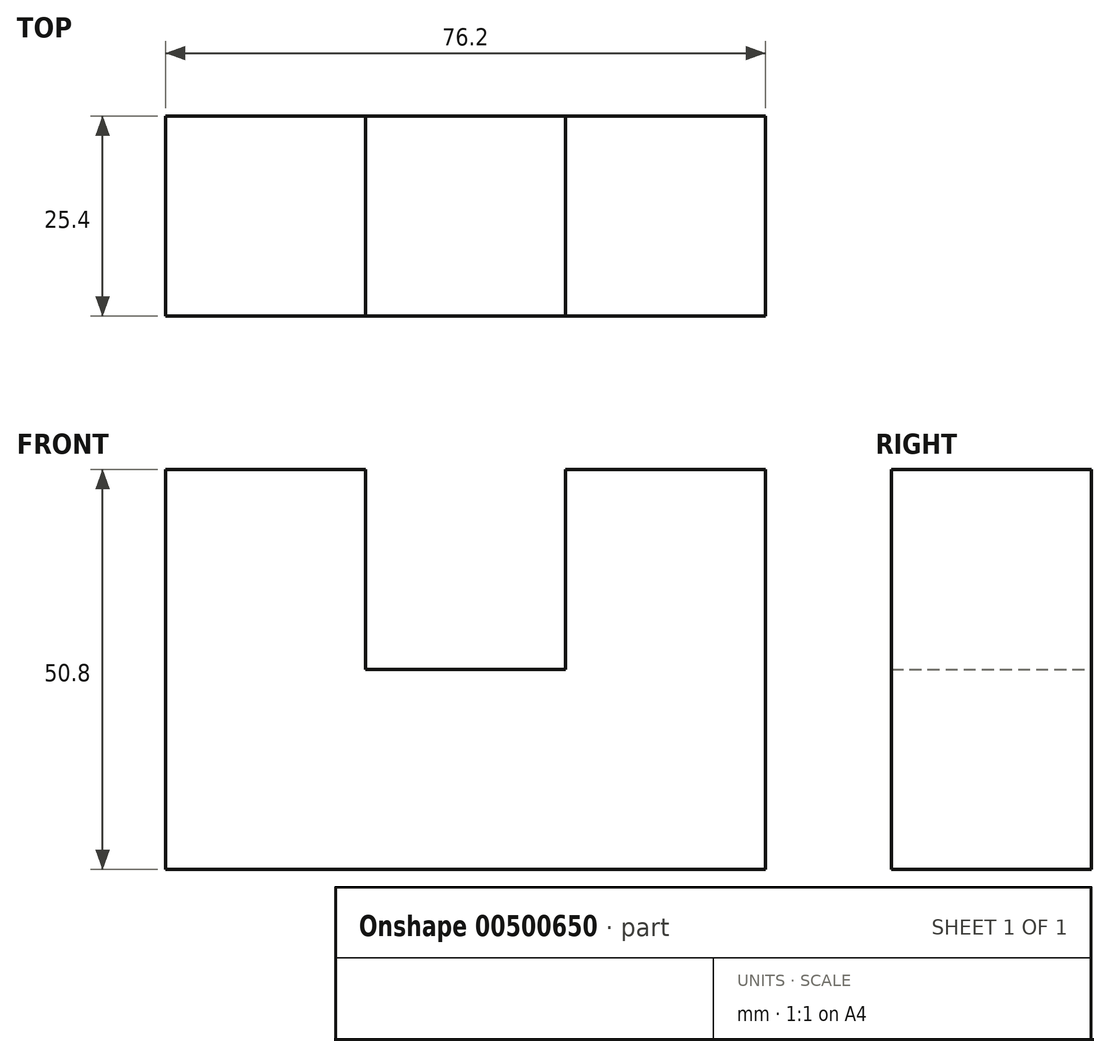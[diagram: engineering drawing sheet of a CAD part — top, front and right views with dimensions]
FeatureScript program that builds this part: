
annotation { "Feature Type Name" : "Feature", "Feature Type Description" : "" }
export const myFeature = defineFeature(function(context is Context, id is Id, definition is map)
    precondition{}
    {
        {
            var Q0;
            Q0=qCreatedBy(makeId("Front.planeOp"),FACE);
            var sketch = newSketch(context, id + "F0", { "sketchPlane" : qUnion([Q0])});
            skLineSegment(sketch, "E0", {"start": v(-5.9, 55.52) * mm, "end": v(19.5, 55.52) * mm});
            skLineSegment(sketch, "E1", {"start": v(19.5, 55.52) * mm, "end": v(19.5, 30.12) * mm});
            skLineSegment(sketch, "E2", {"start": v(19.5, 30.12) * mm, "end": v(44.9, 30.12) * mm});
            skLineSegment(sketch, "E3", {"start": v(44.9, 30.12) * mm, "end": v(44.9, 55.52) * mm});
            skLineSegment(sketch, "E4", {"start": v(44.9, 55.52) * mm, "end": v(70.3, 55.52) * mm});
            skLineSegment(sketch, "E5", {"start": v(-5.9, 55.52) * mm, "end": v(-5.9, 4.72) * mm});
            skLineSegment(sketch, "E6", {"start": v(-5.9, 4.72) * mm, "end": v(70.3, 4.72) * mm});
            skLineSegment(sketch, "E7", {"start": v(70.3, 55.52) * mm, "end": v(70.3, 4.72) * mm});
            skSolve(sketch);
        }
        {
            var Q0;
            Q0 = qSketchRegion(id + "F0", true);
            extrude(context, id + "F1", {"entities" : qUnion([Q0]), "depth" : 25.4 * mm});
        }
    });
